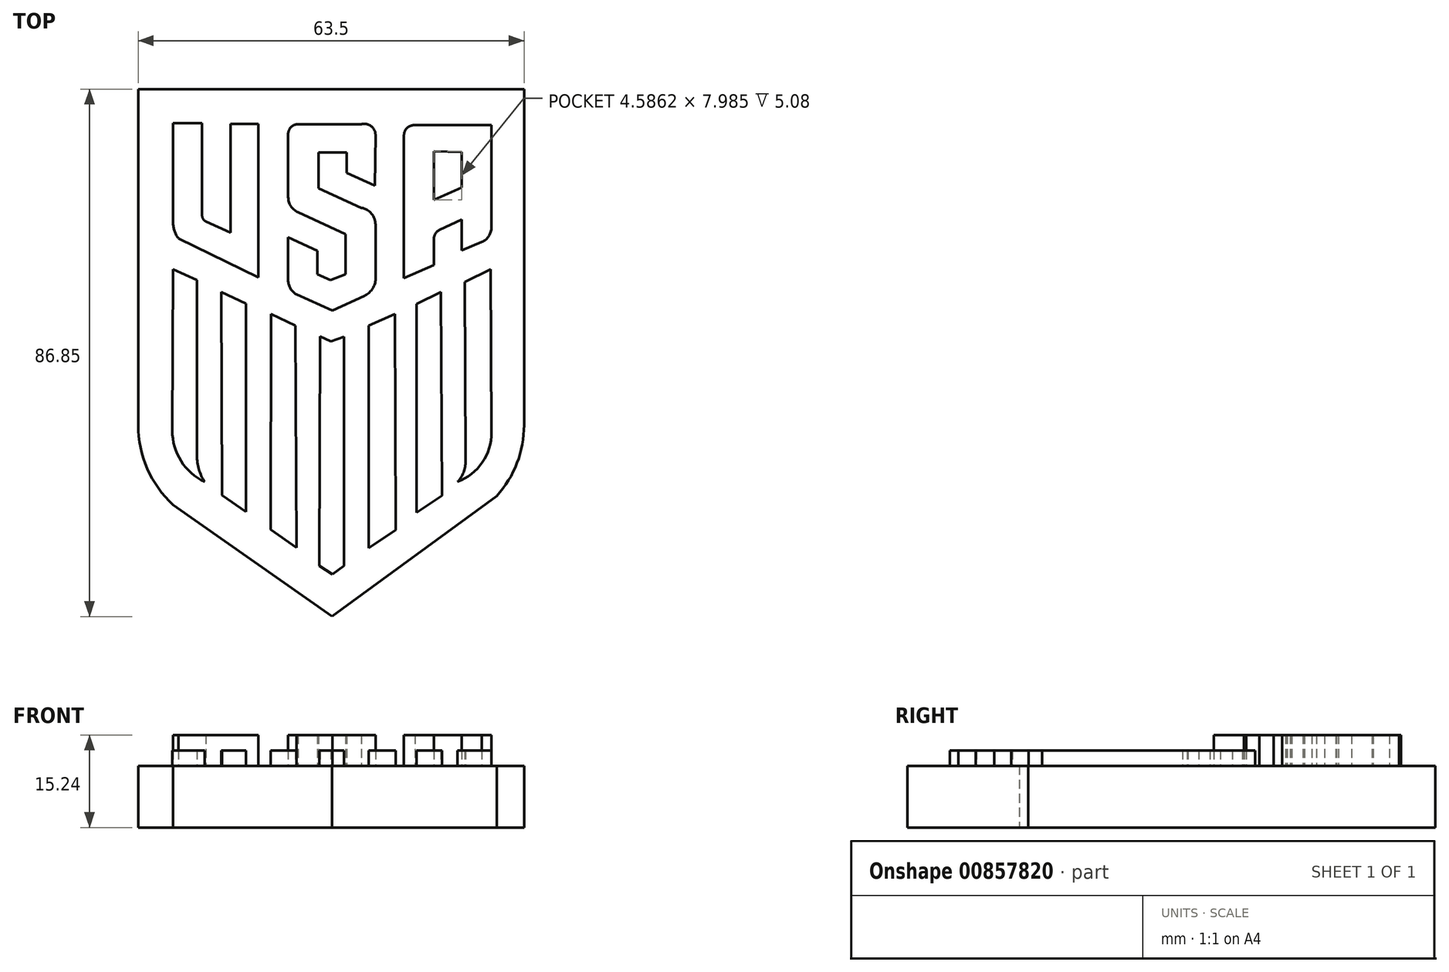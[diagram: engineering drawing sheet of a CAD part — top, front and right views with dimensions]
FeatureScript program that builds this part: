
annotation { "Feature Type Name" : "Feature", "Feature Type Description" : "" }
export const myFeature = defineFeature(function(context is Context, id is Id, definition is map)
    precondition{}
    {
        {
            var Q0;
            Q0=qCreatedBy(makeId("Top.planeOp"),FACE);
            var sketch = newSketch(context, id + "F0", { "sketchPlane" : qUnion([Q0])});
            skLineSegment(sketch, "E0", {"start": v(-45.88, 65.74) * mm, "end": v(17.62, 65.74) * mm});
            skLineSegment(sketch, "E1", {"start": v(17.62, 65.74) * mm, "end": v(17.62, 10.42) * mm});
            skLineSegment(sketch, "E2", {"start": v(-45.88, 65.74) * mm, "end": v(-45.88, 10.42) * mm});
            skArc(sketch, "E3", {"start": v(-45.88, 10.42) * mm, "mid": v(-44.38, 3.25) * mm, "end": v(-40.13, -2.72) * mm});
            skArc(sketch, "E4", {"start": v(13.14, -1.26) * mm, "mid": v(16.46, 4.17) * mm, "end": v(17.62, 10.42) * mm});
            skLineSegment(sketch, "E5", {"start": v(-40.13, -2.72) * mm, "end": v(-13.96, -21.1) * mm});
            skLineSegment(sketch, "E6", {"start": v(-13.96, -21.1) * mm, "end": v(13.14, -1.26) * mm});
            skLineSegment(sketch, "E7", {"start": v(-40.13, 60.13) * mm, "end": v(-35.35, 60.13) * mm});
            skLineSegment(sketch, "E8", {"start": v(-35.35, 60.13) * mm, "end": v(-35.35, 44.84) * mm});
            skLineSegment(sketch, "E9", {"start": v(-30.67, 42.3) * mm, "end": v(-30.67, 60.03) * mm});
            skLineSegment(sketch, "E10", {"start": v(-30.67, 60.03) * mm, "end": v(-26.1, 60.03) * mm});
            skLineSegment(sketch, "E11", {"start": v(-26.1, 60.03) * mm, "end": v(-26.1, 34.71) * mm});
            skLineSegment(sketch, "E12", {"start": v(-26.1, 34.71) * mm, "end": v(-39.25, 41.14) * mm});
            skLineSegment(sketch, "E13", {"start": v(-40.13, 60.13) * mm, "end": v(-40.13, 43.77) * mm});
            skArc(sketch, "E14", {"start": v(-40.13, 43.77) * mm, "mid": v(-39.9, 42.38) * mm, "end": v(-39.25, 41.14) * mm});
            skLineSegment(sketch, "E15", {"start": v(-30.67, 42.3) * mm, "end": v(-30.67, 42.13) * mm});
            skLineSegment(sketch, "E16", {"start": v(-30.67, 42.13) * mm, "end": v(-34.74, 43.98) * mm});
            skArc(sketch, "E17", {"start": v(-35.35, 44.84) * mm, "mid": v(-35.18, 44.31) * mm, "end": v(-34.74, 43.98) * mm});
            skLineSegment(sketch, "E18", {"start": v(-6.95, 49.84) * mm, "end": v(-11.58, 51.97) * mm});
            skLineSegment(sketch, "E19", {"start": v(-11.58, 51.97) * mm, "end": v(-11.58, 55.33) * mm});
            skLineSegment(sketch, "E20", {"start": v(-11.58, 55.33) * mm, "end": v(-16.2, 55.33) * mm});
            skLineSegment(sketch, "E21", {"start": v(-16.2, 55.33) * mm, "end": v(-16.2, 49.39) * mm});
            skLineSegment(sketch, "E22", {"start": v(-16.2, 49.39) * mm, "end": v(-9.16, 46.2) * mm});
            skLineSegment(sketch, "E23", {"start": v(-6.83, 43.4) * mm, "end": v(-6.83, 34.28) * mm});
            skLineSegment(sketch, "E24", {"start": v(-8.67, 31.7) * mm, "end": v(-13.91, 29.28) * mm});
            skLineSegment(sketch, "E25", {"start": v(-13.91, 29.28) * mm, "end": v(-19.85, 31.94) * mm});
            skLineSegment(sketch, "E26", {"start": v(-21.2, 34.28) * mm, "end": v(-21.2, 41.36) * mm});
            skLineSegment(sketch, "E27", {"start": v(-21.2, 41.36) * mm, "end": v(-16.37, 39.15) * mm});
            skLineSegment(sketch, "E28", {"start": v(-16.37, 39.15) * mm, "end": v(-16.37, 35.22) * mm});
            skLineSegment(sketch, "E29", {"start": v(-16.37, 35.22) * mm, "end": v(-14.24, 34.28) * mm});
            skLineSegment(sketch, "E30", {"start": v(-14.24, 34.28) * mm, "end": v(-11.79, 35.22) * mm});
            skLineSegment(sketch, "E31", {"start": v(-11.79, 35.22) * mm, "end": v(-11.79, 41.85) * mm});
            skLineSegment(sketch, "E32", {"start": v(-11.79, 41.85) * mm, "end": v(-19.57, 45.46) * mm});
            skLineSegment(sketch, "E33", {"start": v(-21.2, 47.98) * mm, "end": v(-21.2, 58.17) * mm});
            skLineSegment(sketch, "E34", {"start": v(-19.57, 59.97) * mm, "end": v(-9.16, 59.97) * mm});
            skLineSegment(sketch, "E35", {"start": v(-6.83, 58.17) * mm, "end": v(-6.95, 49.84) * mm});
            skArc(sketch, "E36", {"start": v(-6.83, 58.17) * mm, "mid": v(-7.55, 59.65) * mm, "end": v(-9.16, 59.97) * mm});
            skArc(sketch, "E37", {"start": v(-19.57, 59.97) * mm, "mid": v(-20.78, 59.43) * mm, "end": v(-21.2, 58.17) * mm});
            skArc(sketch, "E38", {"start": v(-21.2, 47.98) * mm, "mid": v(-20.75, 46.48) * mm, "end": v(-19.57, 45.46) * mm});
            skArc(sketch, "E39", {"start": v(-6.83, 43.4) * mm, "mid": v(-7.5, 45.23) * mm, "end": v(-9.16, 46.2) * mm});
            skArc(sketch, "E40", {"start": v(-8.67, 31.7) * mm, "mid": v(-7.4, 32.74) * mm, "end": v(-6.83, 34.28) * mm});
            skArc(sketch, "E41", {"start": v(-21.2, 34.28) * mm, "mid": v(-20.84, 32.93) * mm, "end": v(-19.85, 31.94) * mm});
            skLineSegment(sketch, "E42", {"start": v(2.78, 55.5) * mm, "end": v(2.78, 47.52) * mm});
            skLineSegment(sketch, "E43", {"start": v(2.78, 47.52) * mm, "end": v(7.37, 49.52) * mm});
            skLineSegment(sketch, "E44", {"start": v(7.37, 49.52) * mm, "end": v(7.37, 55.38) * mm});
            skLineSegment(sketch, "E45", {"start": v(7.37, 55.38) * mm, "end": v(2.78, 55.5) * mm});
            skLineSegment(sketch, "E46", {"start": v(2.78, 36.79) * mm, "end": v(2.78, 41.13) * mm});
            skLineSegment(sketch, "E47", {"start": v(3.68, 42.52) * mm, "end": v(7.37, 44.24) * mm});
            skLineSegment(sketch, "E48", {"start": v(7.37, 44.24) * mm, "end": v(7.37, 39.16) * mm});
            skLineSegment(sketch, "E49", {"start": v(7.37, 39.16) * mm, "end": v(10.69, 40.55) * mm});
            skLineSegment(sketch, "E50", {"start": v(12.24, 43.01) * mm, "end": v(12.24, 59.8) * mm});
            skLineSegment(sketch, "E51", {"start": v(12.24, 59.8) * mm, "end": v(-0.32, 59.8) * mm});
            skLineSegment(sketch, "E52", {"start": v(-2.14, 58.14) * mm, "end": v(-2.14, 34.62) * mm});
            skLineSegment(sketch, "E53", {"start": v(-2.14, 34.62) * mm, "end": v(2.78, 36.79) * mm});
            skArc(sketch, "E54", {"start": v(-0.32, 59.8) * mm, "mid": v(-1.6, 59.37) * mm, "end": v(-2.14, 58.14) * mm});
            skArc(sketch, "E55", {"start": v(3.68, 42.52) * mm, "mid": v(3.03, 41.95) * mm, "end": v(2.78, 41.13) * mm});
            skArc(sketch, "E56", {"start": v(10.69, 40.55) * mm, "mid": v(11.82, 41.56) * mm, "end": v(12.24, 43.01) * mm});
            skLineSegment(sketch, "E57", {"start": v(-40.12, 36.1) * mm, "end": v(-36.22, 34.3) * mm});
            skLineSegment(sketch, "E58", {"start": v(-36.22, 34.3) * mm, "end": v(-36.22, 5.38) * mm});
            skLineSegment(sketch, "E59", {"start": v(-40.26, 9.52) * mm, "end": v(-40.12, 36.1) * mm});
            skLineSegment(sketch, "E60", {"start": v(-32.23, 32.35) * mm, "end": v(-28.14, 30.4) * mm});
            skLineSegment(sketch, "E61", {"start": v(-28.14, 30.4) * mm, "end": v(-28.14, -3.85) * mm});
            skLineSegment(sketch, "E62", {"start": v(-28.14, -3.85) * mm, "end": v(-32.05, -1.12) * mm});
            skLineSegment(sketch, "E63", {"start": v(-32.05, -1.12) * mm, "end": v(-32.23, 32.35) * mm});
            skLineSegment(sketch, "E64", {"start": v(-24.02, 28.7) * mm, "end": v(-20.03, 26.8) * mm});
            skLineSegment(sketch, "E65", {"start": v(-20.03, 26.8) * mm, "end": v(-19.83, -9.77) * mm});
            skLineSegment(sketch, "E66", {"start": v(-19.83, -9.77) * mm, "end": v(-24.07, -6.8) * mm});
            skLineSegment(sketch, "E67", {"start": v(-24.07, -6.8) * mm, "end": v(-24.02, 28.7) * mm});
            skLineSegment(sketch, "E68", {"start": v(-15.98, 25.05) * mm, "end": v(-14.17, 24.19) * mm});
            skLineSegment(sketch, "E69", {"start": v(-14.17, 24.19) * mm, "end": v(-12, 24.95) * mm});
            skLineSegment(sketch, "E70", {"start": v(-12, 24.95) * mm, "end": v(-12, -12.73) * mm});
            skLineSegment(sketch, "E71", {"start": v(-12, -12.73) * mm, "end": v(-13.92, -14.15) * mm});
            skLineSegment(sketch, "E72", {"start": v(-13.92, -14.15) * mm, "end": v(-16.05, -12.73) * mm});
            skLineSegment(sketch, "E73", {"start": v(-16.05, -12.73) * mm, "end": v(-15.98, 25.05) * mm});
            skLineSegment(sketch, "E74", {"start": v(-7.95, 26.8) * mm, "end": v(-3.66, 28.7) * mm});
            skLineSegment(sketch, "E75", {"start": v(-3.66, 28.7) * mm, "end": v(-3.48, -6.83) * mm});
            skLineSegment(sketch, "E76", {"start": v(-3.48, -6.83) * mm, "end": v(-7.95, -9.85) * mm});
            skLineSegment(sketch, "E77", {"start": v(-7.95, -9.85) * mm, "end": v(-7.95, 26.8) * mm});
            skLineSegment(sketch, "E78", {"start": v(-0.06, 30.37) * mm, "end": v(3.93, 32.35) * mm});
            skLineSegment(sketch, "E79", {"start": v(3.93, 32.35) * mm, "end": v(4.1, -1.18) * mm});
            skLineSegment(sketch, "E80", {"start": v(4.1, -1.18) * mm, "end": v(-0.06, -4) * mm});
            skLineSegment(sketch, "E81", {"start": v(-0.06, -4) * mm, "end": v(-0.06, 30.37) * mm});
            skLineSegment(sketch, "E82", {"start": v(7.83, 33.97) * mm, "end": v(12.12, 36.1) * mm});
            skLineSegment(sketch, "E83", {"start": v(12.12, 36.1) * mm, "end": v(12.26, 9.24) * mm});
            skLineSegment(sketch, "E84", {"start": v(7.83, 33.97) * mm, "end": v(7.98, 4.47) * mm});
            skArc(sketch, "E85", {"start": v(-40.26, 9.52) * mm, "mid": v(-38.83, 4.5) * mm, "end": v(-34.92, 1.06) * mm});
            skArc(sketch, "E86", {"start": v(-36.22, 5.38) * mm, "mid": v(-35.9, 3.12) * mm, "end": v(-34.92, 1.06) * mm});
            skArc(sketch, "E87", {"start": v(6.66, 1.06) * mm, "mid": v(7.65, 2.64) * mm, "end": v(7.98, 4.47) * mm});
            skArc(sketch, "E88", {"start": v(6.66, 1.06) * mm, "mid": v(10.74, 4.27) * mm, "end": v(12.26, 9.24) * mm});
            skSolve(sketch);
        }
        {
            var Q0;
            Q0=makeQuery(id+"F0.imprint","IMPRINT",FACE,{"disambiguationData":[TD([[makeQuery(id+"F0.imprint","IMPRINT",EDGE,{"derivedFrom":sQuery(id+"F0.wireOp",EDGE,"E7")}),-1.0]])]});
            var Q1;
            Q1=makeQuery(id+"F0.imprint","IMPRINT",FACE,{"disambiguationData":[TD([[makeQuery(id+"F0.imprint","IMPRINT",EDGE,{"derivedFrom":sQuery(id+"F0.wireOp",EDGE,"E18")}),-1.0]])]});
            var Q2;
            Q2=makeQuery(id+"F0.imprint","IMPRINT",FACE,{"disambiguationData":[TD([[makeQuery(id+"F0.imprint","IMPRINT",EDGE,{"derivedFrom":sQuery(id+"F0.wireOp",EDGE,"E42")}),-1.0]])]});
            extrude(context, id + "F1", {"entities" : qUnion([Q0, Q1, Q2]), "depth" : 15.24 * mm, "offsetDistance" : 25.4 * mm});
        }
        {
            var Q0;
            Q0=makeQuery(id+"F0.imprint","IMPRINT",FACE,{"disambiguationData":[TD([[makeQuery(id+"F0.imprint","IMPRINT",EDGE,{"derivedFrom":sQuery(id+"F0.wireOp",EDGE,"E57")}),-1.0]])]});
            var Q1;
            Q1=makeQuery(id+"F0.imprint","IMPRINT",FACE,{"disambiguationData":[TD([[makeQuery(id+"F0.imprint","IMPRINT",EDGE,{"derivedFrom":sQuery(id+"F0.wireOp",EDGE,"E60")}),-1.0]])]});
            var Q2;
            Q2=makeQuery(id+"F0.imprint","IMPRINT",FACE,{"disambiguationData":[TD([[makeQuery(id+"F0.imprint","IMPRINT",EDGE,{"derivedFrom":sQuery(id+"F0.wireOp",EDGE,"E64")}),-1.0]])]});
            var Q3;
            Q3=makeQuery(id+"F0.imprint","IMPRINT",FACE,{"disambiguationData":[TD([[makeQuery(id+"F0.imprint","IMPRINT",EDGE,{"derivedFrom":sQuery(id+"F0.wireOp",EDGE,"E68")}),-1.0]])]});
            var Q4;
            Q4=makeQuery(id+"F0.imprint","IMPRINT",FACE,{"disambiguationData":[TD([[makeQuery(id+"F0.imprint","IMPRINT",EDGE,{"derivedFrom":sQuery(id+"F0.wireOp",EDGE,"E74")}),-1.0]])]});
            var Q5;
            Q5=makeQuery(id+"F0.imprint","IMPRINT",FACE,{"disambiguationData":[TD([[makeQuery(id+"F0.imprint","IMPRINT",EDGE,{"derivedFrom":sQuery(id+"F0.wireOp",EDGE,"E78")}),-1.0]])]});
            var Q6;
            Q6=makeQuery(id+"F0.imprint","IMPRINT",FACE,{"disambiguationData":[TD([[makeQuery(id+"F0.imprint","IMPRINT",EDGE,{"derivedFrom":sQuery(id+"F0.wireOp",EDGE,"E82")}),-1.0]])]});
            extrude(context, id + "F2", {"entities" : qUnion([Q0, Q1, Q2, Q3, Q4, Q5, Q6]), "depth" : 12.7 * mm, "offsetDistance" : 25.4 * mm});
        }
        {
            var Q0;
            Q0=makeQuery(id+"F0.imprint","IMPRINT",FACE,{"disambiguationData":[TD([[makeQuery(id+"F0.imprint","IMPRINT",EDGE,{"derivedFrom":sQuery(id+"F0.wireOp",EDGE,"E0")}),-1.0]])]});
            var Q1;
            Q1=makeQuery(id+"F0.imprint","IMPRINT",FACE,{"disambiguationData":[TD([[makeQuery(id+"F0.imprint","IMPRINT",EDGE,{"derivedFrom":sQuery(id+"F0.wireOp",EDGE,"E42")}),1.0]])]});
            extrude(context, id + "F3", {"entities" : qUnion([Q0, Q1]), "depth" : 10.16 * mm, "offsetDistance" : 25.4 * mm});
        }
        {
            var Q0;
            Q0=makeQuery(id+"F2.opExtrude","SWEPT_BODY",BODY,{"disambiguationData":[OSD([sQuery(id+"F0.wireOp",EDGE,"E57"),sQuery(id+"F0.wireOp",EDGE,"E58"),sQuery(id+"F0.wireOp",EDGE,"E59"),sQuery(id+"F0.wireOp",EDGE,"E85"),sQuery(id+"F0.wireOp",EDGE,"E86")])]});
            var Q1;
            Q1=makeQuery(id+"F2.opExtrude","SWEPT_BODY",BODY,{"disambiguationData":[OSD([sQuery(id+"F0.wireOp",EDGE,"E60"),sQuery(id+"F0.wireOp",EDGE,"E61"),sQuery(id+"F0.wireOp",EDGE,"E62"),sQuery(id+"F0.wireOp",EDGE,"E63")])]});
            var Q2;
            Q2=makeQuery(id+"F2.opExtrude","SWEPT_BODY",BODY,{"disambiguationData":[OSD([sQuery(id+"F0.wireOp",EDGE,"E64"),sQuery(id+"F0.wireOp",EDGE,"E65"),sQuery(id+"F0.wireOp",EDGE,"E66"),sQuery(id+"F0.wireOp",EDGE,"E67")])]});
            var Q3;
            Q3=makeQuery(id+"F2.opExtrude","SWEPT_BODY",BODY,{"disambiguationData":[OSD([sQuery(id+"F0.wireOp",EDGE,"E68"),sQuery(id+"F0.wireOp",EDGE,"E69"),sQuery(id+"F0.wireOp",EDGE,"E70"),sQuery(id+"F0.wireOp",EDGE,"E71"),sQuery(id+"F0.wireOp",EDGE,"E72"),sQuery(id+"F0.wireOp",EDGE,"E73")])]});
            var Q4;
            Q4=makeQuery(id+"F2.opExtrude","SWEPT_BODY",BODY,{"disambiguationData":[OSD([sQuery(id+"F0.wireOp",EDGE,"E78"),sQuery(id+"F0.wireOp",EDGE,"E79"),sQuery(id+"F0.wireOp",EDGE,"E80"),sQuery(id+"F0.wireOp",EDGE,"E81")])]});
            var Q5;
            Q5=makeQuery(id+"F2.opExtrude","SWEPT_BODY",BODY,{"disambiguationData":[OSD([sQuery(id+"F0.wireOp",EDGE,"E82"),sQuery(id+"F0.wireOp",EDGE,"E83"),sQuery(id+"F0.wireOp",EDGE,"E84"),sQuery(id+"F0.wireOp",EDGE,"E87"),sQuery(id+"F0.wireOp",EDGE,"E88")])]});
            var Q6;
            Q6=makeQuery(id+"F3.opExtrude","SWEPT_BODY",BODY,{"disambiguationData":[OSD([sQuery(id+"F0.wireOp",EDGE,"E0"),sQuery(id+"F0.wireOp",EDGE,"E1"),sQuery(id+"F0.wireOp",EDGE,"E2"),sQuery(id+"F0.wireOp",EDGE,"E3"),sQuery(id+"F0.wireOp",EDGE,"E4"),sQuery(id+"F0.wireOp",EDGE,"E5"),sQuery(id+"F0.wireOp",EDGE,"E6"),sQuery(id+"F0.wireOp",EDGE,"E7"),sQuery(id+"F0.wireOp",EDGE,"E8"),sQuery(id+"F0.wireOp",EDGE,"E9"),sQuery(id+"F0.wireOp",EDGE,"E10"),sQuery(id+"F0.wireOp",EDGE,"E11"),sQuery(id+"F0.wireOp",EDGE,"E12"),sQuery(id+"F0.wireOp",EDGE,"E13"),sQuery(id+"F0.wireOp",EDGE,"E14"),sQuery(id+"F0.wireOp",EDGE,"E15"),sQuery(id+"F0.wireOp",EDGE,"E16"),sQuery(id+"F0.wireOp",EDGE,"E17"),sQuery(id+"F0.wireOp",EDGE,"E18"),sQuery(id+"F0.wireOp",EDGE,"E19"),sQuery(id+"F0.wireOp",EDGE,"E20"),sQuery(id+"F0.wireOp",EDGE,"E21"),sQuery(id+"F0.wireOp",EDGE,"E22"),sQuery(id+"F0.wireOp",EDGE,"E23"),sQuery(id+"F0.wireOp",EDGE,"E24"),sQuery(id+"F0.wireOp",EDGE,"E25"),sQuery(id+"F0.wireOp",EDGE,"E26"),sQuery(id+"F0.wireOp",EDGE,"E27"),sQuery(id+"F0.wireOp",EDGE,"E28"),sQuery(id+"F0.wireOp",EDGE,"E29"),sQuery(id+"F0.wireOp",EDGE,"E30"),sQuery(id+"F0.wireOp",EDGE,"E31"),sQuery(id+"F0.wireOp",EDGE,"E32"),sQuery(id+"F0.wireOp",EDGE,"E33"),sQuery(id+"F0.wireOp",EDGE,"E34"),sQuery(id+"F0.wireOp",EDGE,"E35"),sQuery(id+"F0.wireOp",EDGE,"E36"),sQuery(id+"F0.wireOp",EDGE,"E37"),sQuery(id+"F0.wireOp",EDGE,"E38"),sQuery(id+"F0.wireOp",EDGE,"E39"),sQuery(id+"F0.wireOp",EDGE,"E40"),sQuery(id+"F0.wireOp",EDGE,"E41"),sQuery(id+"F0.wireOp",EDGE,"E46"),sQuery(id+"F0.wireOp",EDGE,"E47"),sQuery(id+"F0.wireOp",EDGE,"E48"),sQuery(id+"F0.wireOp",EDGE,"E49"),sQuery(id+"F0.wireOp",EDGE,"E50"),sQuery(id+"F0.wireOp",EDGE,"E51"),sQuery(id+"F0.wireOp",EDGE,"E52"),sQuery(id+"F0.wireOp",EDGE,"E53"),sQuery(id+"F0.wireOp",EDGE,"E54"),sQuery(id+"F0.wireOp",EDGE,"E55"),sQuery(id+"F0.wireOp",EDGE,"E56"),sQuery(id+"F0.wireOp",EDGE,"E57"),sQuery(id+"F0.wireOp",EDGE,"E58"),sQuery(id+"F0.wireOp",EDGE,"E59"),sQuery(id+"F0.wireOp",EDGE,"E60"),sQuery(id+"F0.wireOp",EDGE,"E61"),sQuery(id+"F0.wireOp",EDGE,"E62"),sQuery(id+"F0.wireOp",EDGE,"E63"),sQuery(id+"F0.wireOp",EDGE,"E64"),sQuery(id+"F0.wireOp",EDGE,"E65"),sQuery(id+"F0.wireOp",EDGE,"E66"),sQuery(id+"F0.wireOp",EDGE,"E67"),sQuery(id+"F0.wireOp",EDGE,"E68"),sQuery(id+"F0.wireOp",EDGE,"E69"),sQuery(id+"F0.wireOp",EDGE,"E70"),sQuery(id+"F0.wireOp",EDGE,"E71"),sQuery(id+"F0.wireOp",EDGE,"E72"),sQuery(id+"F0.wireOp",EDGE,"E73"),sQuery(id+"F0.wireOp",EDGE,"E74"),sQuery(id+"F0.wireOp",EDGE,"E75"),sQuery(id+"F0.wireOp",EDGE,"E76"),sQuery(id+"F0.wireOp",EDGE,"E77"),sQuery(id+"F0.wireOp",EDGE,"E78"),sQuery(id+"F0.wireOp",EDGE,"E79"),sQuery(id+"F0.wireOp",EDGE,"E80"),sQuery(id+"F0.wireOp",EDGE,"E81"),sQuery(id+"F0.wireOp",EDGE,"E82"),sQuery(id+"F0.wireOp",EDGE,"E83"),sQuery(id+"F0.wireOp",EDGE,"E84"),sQuery(id+"F0.wireOp",EDGE,"E85"),sQuery(id+"F0.wireOp",EDGE,"E86"),sQuery(id+"F0.wireOp",EDGE,"E87"),sQuery(id+"F0.wireOp",EDGE,"E88")])]});
            booleanBodies(context, id + "F4", {"operationType" : BooleanOperationType.UNION, "tools" : qUnion([Q0, Q1, Q2, Q3, Q4, Q5, Q6])});
        }
        {
            var Q0;
            Q0=makeQuery(id+"F2.opExtrude","SWEPT_BODY",BODY,{"disambiguationData":[OSD([sQuery(id+"F0.wireOp",EDGE,"E74"),sQuery(id+"F0.wireOp",EDGE,"E75"),sQuery(id+"F0.wireOp",EDGE,"E76"),sQuery(id+"F0.wireOp",EDGE,"E77")])]});
            var Q1;
            Q1=makeQuery(id+"F2.opExtrude","SWEPT_BODY",BODY,{"disambiguationData":[OSD([sQuery(id+"F0.wireOp",EDGE,"E57"),sQuery(id+"F0.wireOp",EDGE,"E58"),sQuery(id+"F0.wireOp",EDGE,"E59"),sQuery(id+"F0.wireOp",EDGE,"E85"),sQuery(id+"F0.wireOp",EDGE,"E86")])]});
            booleanBodies(context, id + "F5", {"operationType" : BooleanOperationType.UNION, "tools" : qUnion([Q0, Q1])});
        }
        {
            var Q0;
            Q0=makeQuery(id+"F1.opExtrude","SWEPT_BODY",BODY,{"disambiguationData":[OSD([sQuery(id+"F0.wireOp",EDGE,"E7"),sQuery(id+"F0.wireOp",EDGE,"E8"),sQuery(id+"F0.wireOp",EDGE,"E9"),sQuery(id+"F0.wireOp",EDGE,"E10"),sQuery(id+"F0.wireOp",EDGE,"E11"),sQuery(id+"F0.wireOp",EDGE,"E12"),sQuery(id+"F0.wireOp",EDGE,"E13"),sQuery(id+"F0.wireOp",EDGE,"E14"),sQuery(id+"F0.wireOp",EDGE,"E15"),sQuery(id+"F0.wireOp",EDGE,"E16"),sQuery(id+"F0.wireOp",EDGE,"E17")])]});
            var Q1;
            Q1=makeQuery(id+"F1.opExtrude","SWEPT_BODY",BODY,{"disambiguationData":[OSD([sQuery(id+"F0.wireOp",EDGE,"E18"),sQuery(id+"F0.wireOp",EDGE,"E19"),sQuery(id+"F0.wireOp",EDGE,"E20"),sQuery(id+"F0.wireOp",EDGE,"E21"),sQuery(id+"F0.wireOp",EDGE,"E22"),sQuery(id+"F0.wireOp",EDGE,"E23"),sQuery(id+"F0.wireOp",EDGE,"E24"),sQuery(id+"F0.wireOp",EDGE,"E25"),sQuery(id+"F0.wireOp",EDGE,"E26"),sQuery(id+"F0.wireOp",EDGE,"E27"),sQuery(id+"F0.wireOp",EDGE,"E28"),sQuery(id+"F0.wireOp",EDGE,"E29"),sQuery(id+"F0.wireOp",EDGE,"E30"),sQuery(id+"F0.wireOp",EDGE,"E31"),sQuery(id+"F0.wireOp",EDGE,"E32"),sQuery(id+"F0.wireOp",EDGE,"E33"),sQuery(id+"F0.wireOp",EDGE,"E34"),sQuery(id+"F0.wireOp",EDGE,"E35"),sQuery(id+"F0.wireOp",EDGE,"E36"),sQuery(id+"F0.wireOp",EDGE,"E37"),sQuery(id+"F0.wireOp",EDGE,"E38"),sQuery(id+"F0.wireOp",EDGE,"E39"),sQuery(id+"F0.wireOp",EDGE,"E40"),sQuery(id+"F0.wireOp",EDGE,"E41")])]});
            var Q2;
            Q2=makeQuery(id+"F1.opExtrude","SWEPT_BODY",BODY,{"disambiguationData":[OSD([sQuery(id+"F0.wireOp",EDGE,"E42"),sQuery(id+"F0.wireOp",EDGE,"E43"),sQuery(id+"F0.wireOp",EDGE,"E44"),sQuery(id+"F0.wireOp",EDGE,"E45"),sQuery(id+"F0.wireOp",EDGE,"E46"),sQuery(id+"F0.wireOp",EDGE,"E47"),sQuery(id+"F0.wireOp",EDGE,"E48"),sQuery(id+"F0.wireOp",EDGE,"E49"),sQuery(id+"F0.wireOp",EDGE,"E50"),sQuery(id+"F0.wireOp",EDGE,"E51"),sQuery(id+"F0.wireOp",EDGE,"E52"),sQuery(id+"F0.wireOp",EDGE,"E53"),sQuery(id+"F0.wireOp",EDGE,"E54"),sQuery(id+"F0.wireOp",EDGE,"E55"),sQuery(id+"F0.wireOp",EDGE,"E56")])]});
            var Q3;
            Q3=makeQuery(id+"F3.opExtrude","SWEPT_BODY",BODY,{"disambiguationData":[OSD([sQuery(id+"F0.wireOp",EDGE,"E42"),sQuery(id+"F0.wireOp",EDGE,"E43"),sQuery(id+"F0.wireOp",EDGE,"E44"),sQuery(id+"F0.wireOp",EDGE,"E45")])]});
            var Q4;
            Q4=makeQuery(id+"F2.opExtrude","SWEPT_BODY",BODY,{"disambiguationData":[OSD([sQuery(id+"F0.wireOp",EDGE,"E74"),sQuery(id+"F0.wireOp",EDGE,"E75"),sQuery(id+"F0.wireOp",EDGE,"E76"),sQuery(id+"F0.wireOp",EDGE,"E77")])]});
            booleanBodies(context, id + "F6", {"operationType" : BooleanOperationType.UNION, "tools" : qUnion([Q0, Q1, Q2, Q3, Q4])});
        }
    });
